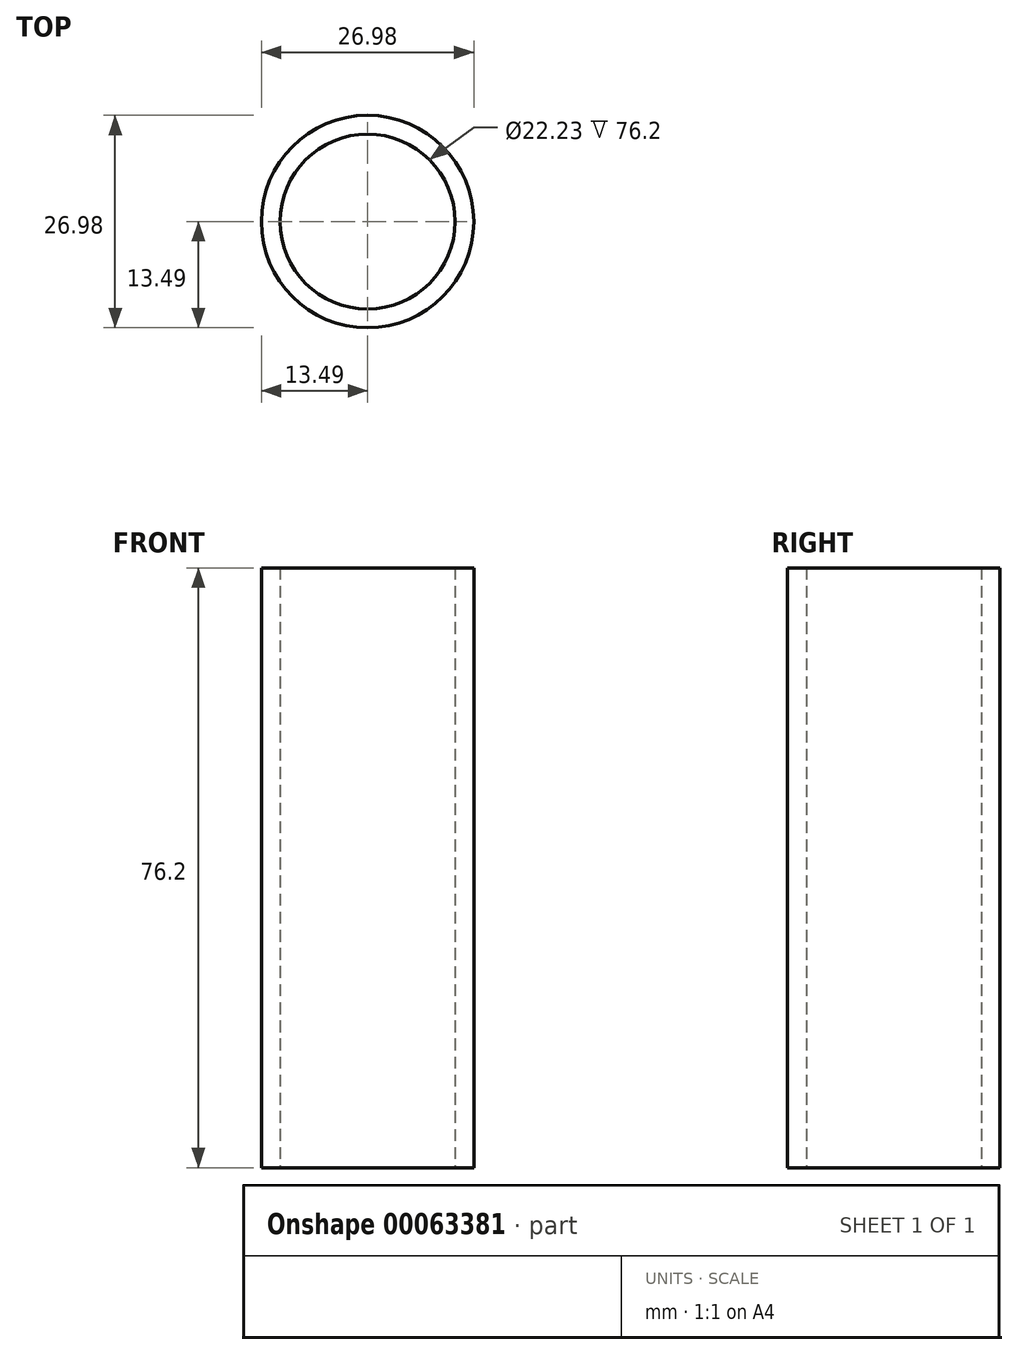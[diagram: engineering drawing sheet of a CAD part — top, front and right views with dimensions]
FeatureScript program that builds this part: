
annotation { "Feature Type Name" : "Feature", "Feature Type Description" : "" }
export const myFeature = defineFeature(function(context is Context, id is Id, definition is map)
    precondition{}
    {
        {
            var Q0;
            Q0=qCreatedBy(makeId("Top.planeOp"),FACE);
            var sketch = newSketch(context, id + "F0", { "sketchPlane" : qUnion([Q0])});
            skCircle(sketch, "E0", {"center": v(0, 0) * mm, "radius": 13.5 * mm});
            skCircle(sketch, "E1", {"center": v(0, 0) * mm, "radius": 11.11 * mm});
            skSolve(sketch);
        }
        {
            var Q0;
            Q0=makeQuery(id+"F0.imprint","IMPRINT",FACE,{"disambiguationData":[TD([[makeQuery(id+"F0.imprint","IMPRINT",EDGE,{"derivedFrom":sQuery(id+"F0.wireOp",EDGE,"E0")}),1.0]])]});
            extrude(context, id + "F1", {"entities" : qUnion([Q0]), "endBound" : BoundingType.SYMMETRIC, "depth" : 76.2 * mm});
        }
    });
